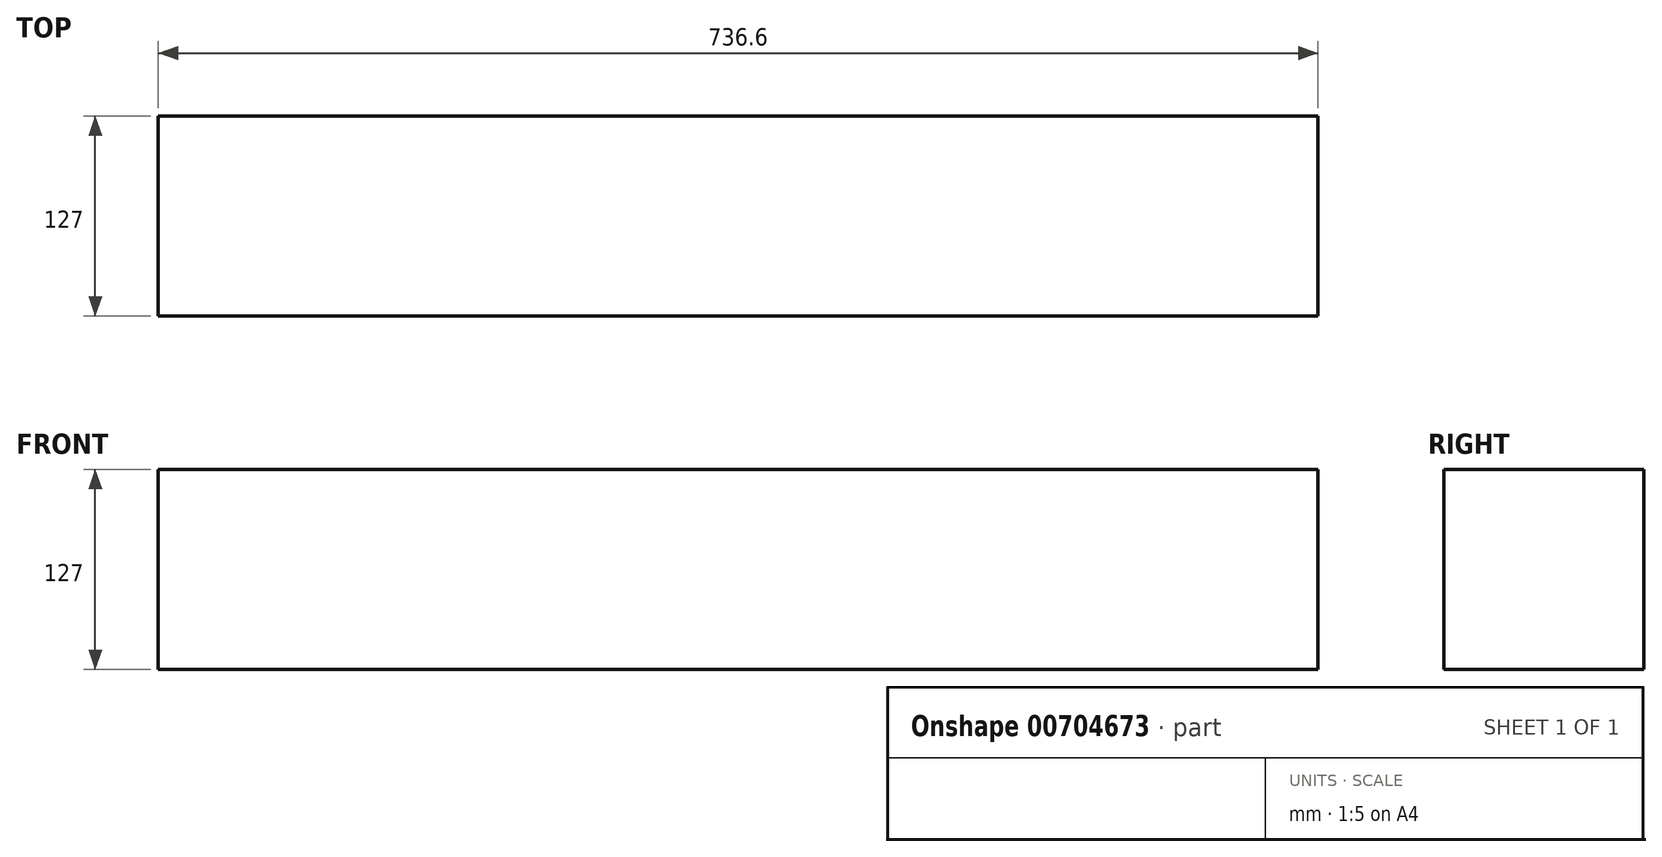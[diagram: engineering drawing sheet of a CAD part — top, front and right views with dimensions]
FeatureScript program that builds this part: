
annotation { "Feature Type Name" : "Feature", "Feature Type Description" : "" }
export const myFeature = defineFeature(function(context is Context, id is Id, definition is map)
    precondition{}
    {
        {
            var Q0;
            Q0=qCreatedBy(makeId("Top.planeOp"),FACE);
            var sketch = newSketch(context, id + "F0", { "sketchPlane" : qUnion([Q0])});
            skLineSegment(sketch, "E0.bottom", {"start": v(173.07, 127) * mm, "end": v(-563.53, 127) * mm});
            skLineSegment(sketch, "E0.top", {"start": v(173.07, 0) * mm, "end": v(-563.53, 0) * mm});
            skLineSegment(sketch, "E0.left", {"start": v(173.07, 127) * mm, "end": v(173.07, 0) * mm});
            skLineSegment(sketch, "E0.right", {"start": v(-563.53, 127) * mm, "end": v(-563.53, 0) * mm});
            skSolve(sketch);
        }
        {
            var Q0;
            Q0=qSketchRegion(id+"F0",true);
            extrude(context, id + "F1", {"entities" : qUnion([Q0]), "depth" : 127 * mm, "offsetDistance" : 25.4 * mm});
        }
    });
